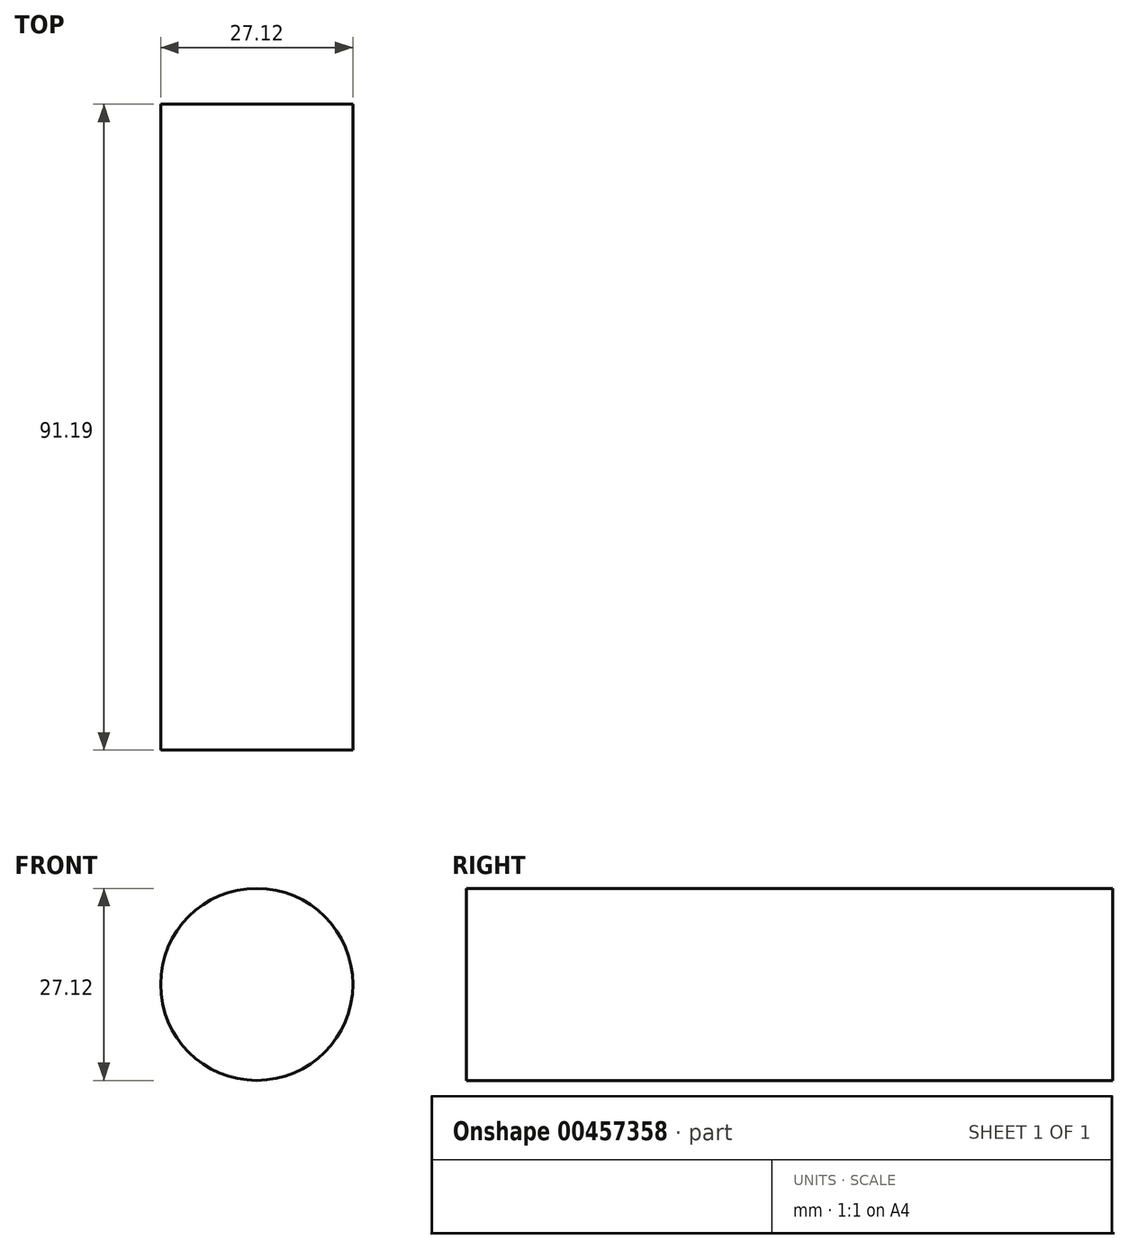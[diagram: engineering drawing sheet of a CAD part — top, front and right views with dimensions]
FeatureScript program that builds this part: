
annotation { "Feature Type Name" : "Feature", "Feature Type Description" : "" }
export const myFeature = defineFeature(function(context is Context, id is Id, definition is map)
    precondition{}
    {
        {
            var Q0;
            Q0=qCreatedBy(makeId("Front.planeOp"),FACE);
            var sketch = newSketch(context, id + "F0", { "sketchPlane" : qUnion([Q0])});
            skCircle(sketch, "E0", {"center": v(0, 0) * mm, "radius": 13.56 * mm});
            skArc(sketch, "E1", {"start": v(22.3, 61.97) * mm, "mid": v(2.35, 68.03) * mm, "end": v(-17.83, 62.86) * mm});
            skSolve(sketch);
        }
        {
            var Q0;
            Q0=makeQuery(id+"F0.imprint","IMPRINT",FACE,{"disambiguationData":[TD([[makeQuery(id+"F0.imprint","IMPRINT",EDGE,{"derivedFrom":sQuery(id+"F0.wireOp",EDGE,"E0")}),1.0]])]});
            extrude(context, id + "F1", {"entities" : qUnion([Q0]), "depth" : 91.19 * mm});
        }
    });
